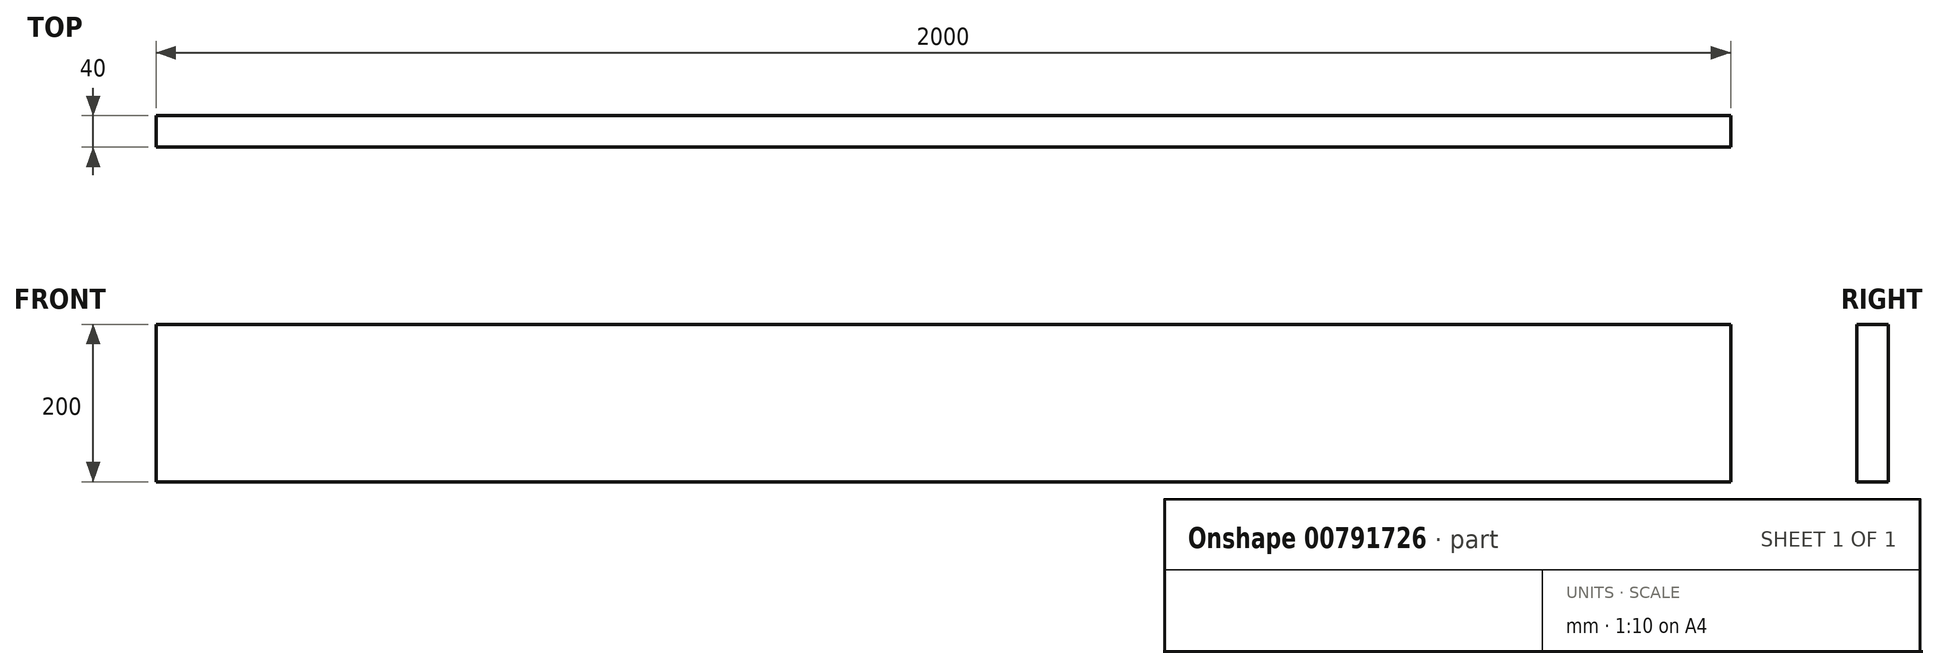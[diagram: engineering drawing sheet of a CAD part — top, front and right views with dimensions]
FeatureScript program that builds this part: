
annotation { "Feature Type Name" : "Feature", "Feature Type Description" : "" }
export const myFeature = defineFeature(function(context is Context, id is Id, definition is map)
    precondition{}
    {
        {
            var Q0;
            Q0=qCreatedBy(makeId("Front.planeOp"),FACE);
            var sketch = newSketch(context, id + "F0", { "sketchPlane" : qUnion([Q0])});
            skLineSegment(sketch, "E0.bottom", {"start": v(-991.87, 27.14) * mm, "end": v(1008.13, 27.14) * mm});
            skLineSegment(sketch, "E0.top", {"start": v(-991.87, -172.86) * mm, "end": v(1008.13, -172.86) * mm});
            skLineSegment(sketch, "E0.left", {"start": v(-991.87, 27.14) * mm, "end": v(-991.87, -172.86) * mm});
            skLineSegment(sketch, "E0.right", {"start": v(1008.13, 27.14) * mm, "end": v(1008.13, -172.86) * mm});
            skLineSegment(sketch, "E1", {"start": v(-951.87, 27.14) * mm, "end": v(-951.87, -172.86) * mm, "construction": true});
            skLineSegment(sketch, "E2", {"start": v(968.13, 27.14) * mm, "end": v(968.13, -172.86) * mm, "construction": true});
            skPoint(sketch, "E3", {"position": v(-971.87, -72.86) * mm});
            skPoint(sketch, "E4", {"position": v(988.13, -72.86) * mm});
            skLineSegment(sketch, "E5", {"start": v(0, 27.14) * mm, "end": v(0, -172.86) * mm, "construction": true});
            skSolve(sketch);
        }
        {
            var Q0;
            Q0 = qSketchRegion(id + "F0", true);
            extrude(context, id + "F1", {"entities" : qUnion([Q0]), "endBound" : BoundingType.SYMMETRIC, "depth" : 40 * mm, "offsetDistance" : 25 * mm});
        }
    });
